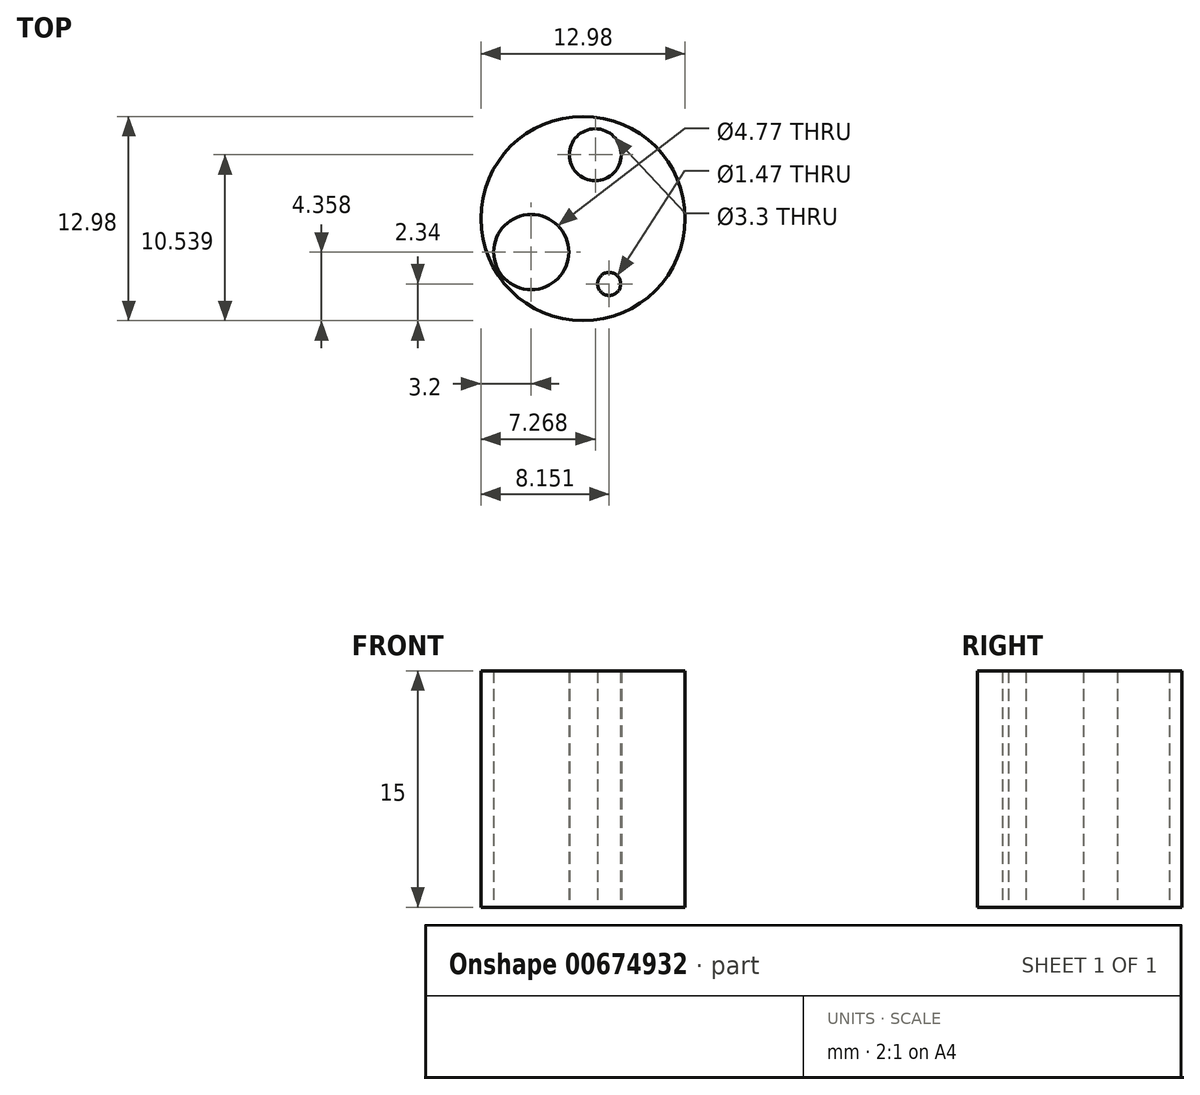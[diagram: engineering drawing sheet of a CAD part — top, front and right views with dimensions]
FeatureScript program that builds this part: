
annotation { "Feature Type Name" : "Feature", "Feature Type Description" : "" }
export const myFeature = defineFeature(function(context is Context, id is Id, definition is map)
    precondition{}
    {
        {
            var Q0;
            Q0=qCreatedBy(makeId("Top.planeOp"),FACE);
            var sketch = newSketch(context, id + "F0", { "sketchPlane" : qUnion([Q0])});
            skCircle(sketch, "E0", {"center": v(0, 0) * mm, "radius": 6.5 * mm});
            skCircle(sketch, "E1", {"center": v(-3.3, -2.13) * mm, "radius": 2.39 * mm});
            skCircle(sketch, "E2", {"center": v(1.66, -4.15) * mm, "radius": 0.73 * mm});
            skCircle(sketch, "E3", {"center": v(0.78, 4.05) * mm, "radius": 1.65 * mm});
            skSolve(sketch);
        }
        {
            var Q0;
            Q0 = qSketchRegion(id + "F0", true);
            extrude(context, id + "F1", {"entities" : qUnion([Q0]), "depth" : 15 * mm, "offsetDistance" : 25 * mm});
        }
    });
